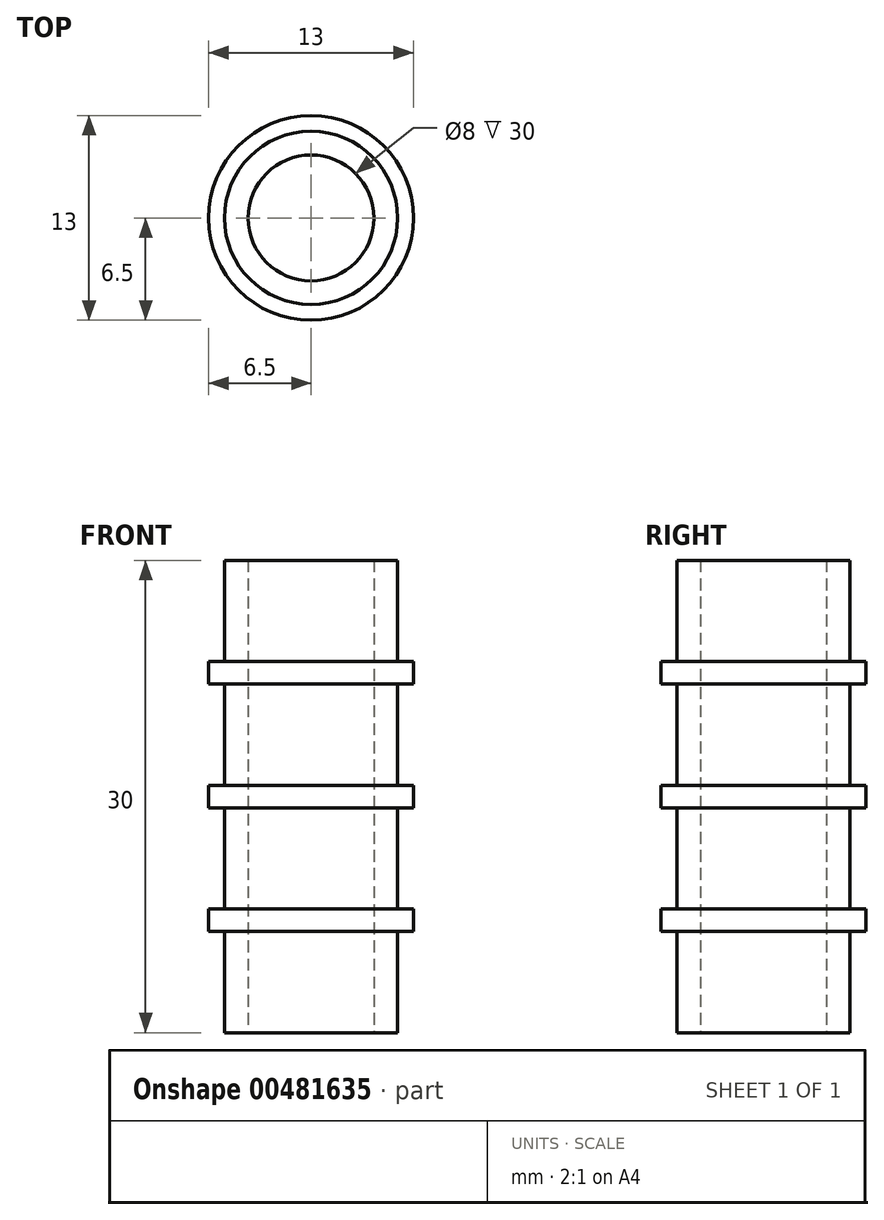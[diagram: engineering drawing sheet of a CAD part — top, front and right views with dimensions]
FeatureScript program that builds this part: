
annotation { "Feature Type Name" : "Feature", "Feature Type Description" : "" }
export const myFeature = defineFeature(function(context is Context, id is Id, definition is map)
    precondition{}
    {
        {
            var Q0;
            Q0=qCreatedBy(makeId("Right.planeOp"),FACE);
            var sketch = newSketch(context, id + "F0", { "sketchPlane" : qUnion([Q0])});
            skLineSegment(sketch, "E0", {"start": v(4, 16.59) * mm, "end": v(4, -13.41) * mm});
            skLineSegment(sketch, "E1", {"start": v(4, -13.41) * mm, "end": v(5.5, -13.41) * mm});
            skLineSegment(sketch, "E2", {"start": v(5.5, -13.41) * mm, "end": v(5.5, -6.99) * mm});
            skLineSegment(sketch, "E3", {"start": v(5.5, -6.99) * mm, "end": v(6.5, -6.99) * mm});
            skLineSegment(sketch, "E4", {"start": v(6.5, -6.99) * mm, "end": v(6.5, -5.55) * mm});
            skLineSegment(sketch, "E5", {"start": v(6.5, -5.55) * mm, "end": v(5.5, -5.55) * mm});
            skLineSegment(sketch, "E6", {"start": v(5.5, -5.55) * mm, "end": v(5.5, 0.87) * mm});
            skLineSegment(sketch, "E7", {"start": v(5.5, 0.87) * mm, "end": v(6.5, 0.87) * mm});
            skLineSegment(sketch, "E8", {"start": v(6.5, 0.87) * mm, "end": v(6.5, 2.3) * mm});
            skLineSegment(sketch, "E9", {"start": v(6.5, 2.3) * mm, "end": v(5.5, 2.3) * mm});
            skLineSegment(sketch, "E10", {"start": v(5.5, 2.3) * mm, "end": v(5.5, 8.73) * mm});
            skLineSegment(sketch, "E11", {"start": v(5.5, 8.73) * mm, "end": v(6.5, 8.73) * mm});
            skLineSegment(sketch, "E12", {"start": v(6.5, 8.73) * mm, "end": v(6.5, 10.16) * mm});
            skLineSegment(sketch, "E13", {"start": v(6.5, 10.16) * mm, "end": v(5.5, 10.16) * mm});
            skLineSegment(sketch, "E14", {"start": v(5.5, 10.16) * mm, "end": v(5.5, 16.59) * mm});
            skLineSegment(sketch, "E15", {"start": v(5.5, 16.59) * mm, "end": v(4, 16.59) * mm});
            skLineSegment(sketch, "E16", {"start": v(0, 0) * mm, "end": v(0, 26.49) * mm, "construction": true});
            skSolve(sketch);
        }
        {
            var Q0;
            Q0 = qSketchRegion(id + "F0", true);
            var Q1;
            Q1=sQuery(id+"F0.wireOp",EDGE,"E16");
            revolve(context, id + "F1", {"entities" : qUnion([Q0]), "axis" : qUnion([Q1]), "revolveType" : RevolveType.FULL});
        }
    });
